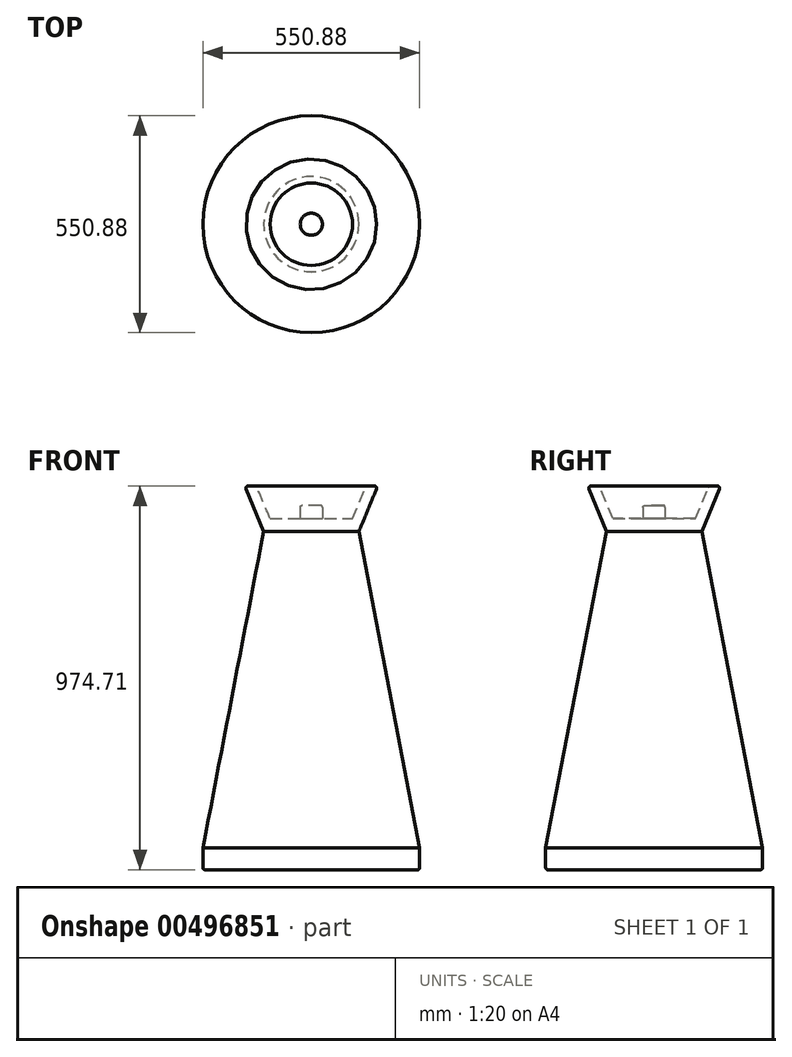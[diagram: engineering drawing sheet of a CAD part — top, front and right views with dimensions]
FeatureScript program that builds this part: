
annotation { "Feature Type Name" : "Feature", "Feature Type Description" : "" }
export const myFeature = defineFeature(function(context is Context, id is Id, definition is map)
    precondition{}
    {
        {
            var Q0;
            Q0=qCreatedBy(makeId("Front.planeOp"),FACE);
            var sketch = newSketch(context, id + "F0", { "sketchPlane" : qUnion([Q0])});
            skLineSegment(sketch, "E0", {"start": v(0, 0) * mm, "end": v(0, 859.48) * mm});
            skLineSegment(sketch, "E1", {"start": v(0, 0) * mm, "end": v(-275.44, 0) * mm});
            skLineSegment(sketch, "E2", {"start": v(-275.44, 0) * mm, "end": v(-275.44, 54.92) * mm});
            skLineSegment(sketch, "E3", {"start": v(-275.44, 54.92) * mm, "end": v(-121, 859.48) * mm});
            skLineSegment(sketch, "E4", {"start": v(-121, 859.48) * mm, "end": v(0, 859.48) * mm});
            skSolve(sketch);
        }
        {
            var Q0;
            Q0=qCreatedBy(makeId("Front.planeOp"),FACE);
            var sketch = newSketch(context, id + "F1", { "sketchPlane" : qUnion([Q0])});
            skLineSegment(sketch, "E5", {"start": v(0, 0) * mm, "end": v(0, 1100.23) * mm});
            skSolve(sketch);
        }
        {
            var Q0;
            Q0=qCreatedBy(makeId("Front.planeOp"),FACE);
            var sketch = newSketch(context, id + "F2", { "sketchPlane" : qUnion([Q0])});
            skLineSegment(sketch, "E6", {"start": v(-120.94, 859.4) * mm, "end": v(-168.6, 974.7) * mm});
            skLineSegment(sketch, "E7", {"start": v(-168.6, 974.7) * mm, "end": v(-139.25, 974.7) * mm});
            skLineSegment(sketch, "E8", {"start": v(-139.25, 974.7) * mm, "end": v(-104.62, 891.97) * mm});
            skLineSegment(sketch, "E9", {"start": v(-104.62, 891.97) * mm, "end": v(-28.13, 891.97) * mm});
            skLineSegment(sketch, "E10", {"start": v(-28.13, 891.97) * mm, "end": v(-28.13, 925.64) * mm});
            skLineSegment(sketch, "E11", {"start": v(-28.13, 925.64) * mm, "end": v(0, 925.64) * mm});
            skLineSegment(sketch, "E12", {"start": v(0, 925.64) * mm, "end": v(0, 859.25) * mm});
            skLineSegment(sketch, "E13", {"start": v(0, 859.25) * mm, "end": v(-120.94, 859.4) * mm});
            skSolve(sketch);
        }
        {
            var Q0;
            Q0 = qSketchRegion(id + "F0", true);
            var Q1;
            Q1=sQuery(id+"F1.wireOp",EDGE,"E5");
            revolve(context, id + "F3", {"entities" : qUnion([Q0]), "axis" : qUnion([Q1]), "revolveType" : RevolveType.FULL});
        }
        {
            var Q0;
            Q0 = qSketchRegion(id + "F2", true);
            var Q1;
            Q1=makeQuery(id+"F2.imprint","IMPRINT",FACE,{"disambiguationData":[TD([[makeQuery(id+"F2.imprint","IMPRINT",EDGE,{"derivedFrom":sQuery(id+"F2.wireOp",EDGE,"E6")}),-1.0]])]});
            var Q2;
            Q2=sQuery(id+"F1.wireOp",EDGE,"E5");
            revolve(context, id + "F4", {"operationType" : NewBodyOperationType.ADD, "entities" : qUnion([Q0, Q1]), "axis" : qUnion([Q2]), "revolveType" : RevolveType.FULL});
        }
        {
            var Q0;
            Q0=makeQuery(id+"F4.opRevolve","SWEPT_EDGE",EDGE,{"disambiguationData":[OSD([sQuery(id+"F2.wireOp",EDGE,"E6"),sQuery(id+"F2.wireOp",EDGE,"E7")])]});
            fillet(context, id + "F5", {"entities" : qUnion([Q0]), "radius" : 5 * mm, "tangentPropagation" : true, "allowEdgeOverflow" : false});
        }
        {
            var Q0;
            Q0=makeQuery(id+"F4.opRevolve","SWEPT_EDGE",EDGE,{"disambiguationData":[OSD([sQuery(id+"F2.wireOp",EDGE,"E7"),sQuery(id+"F2.wireOp",EDGE,"E8")])]});
            fillet(context, id + "F6", {"entities" : qUnion([Q0]), "radius" : 5 * mm, "tangentPropagation" : true, "allowEdgeOverflow" : false});
        }
        {
            var Q0;
            Q0=makeQuery(id+"F4.opRevolve","SWEPT_EDGE",EDGE,{"disambiguationData":[OSD([sQuery(id+"F2.wireOp",EDGE,"E10"),sQuery(id+"F2.wireOp",EDGE,"E11")])]});
            fillet(context, id + "F7", {"entities" : qUnion([Q0]), "radius" : 5 * mm, "tangentPropagation" : true, "allowEdgeOverflow" : false});
        }
        {
            var Q0;
            Q0=makeQuery(id+"F3.opRevolve","SWEPT_EDGE",EDGE,{"disambiguationData":[OSD([sQuery(id+"F0.wireOp",EDGE,"E1"),sQuery(id+"F0.wireOp",EDGE,"E2")])]});
            fillet(context, id + "F8", {"entities" : qUnion([Q0]), "radius" : 5 * mm, "tangentPropagation" : true, "allowEdgeOverflow" : false});
        }
    });
